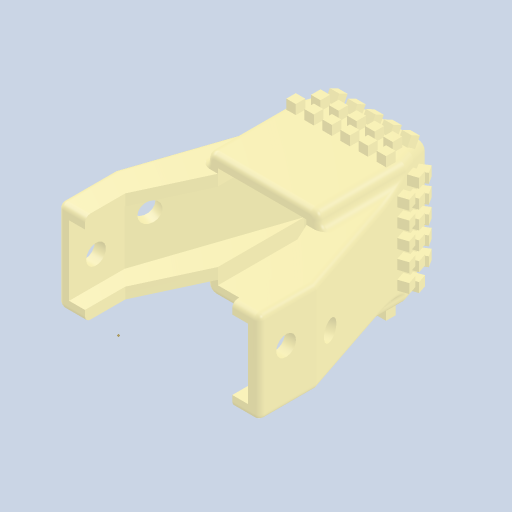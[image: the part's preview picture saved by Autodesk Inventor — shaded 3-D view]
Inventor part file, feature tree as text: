
AUTODESK INVENTOR PART (.ipt)
format: ipt  version: 2023 (Build 270158000, 158)  size: 1,275,904 bytes
history: native  units: mm
features: other x27, extrude x18, fillet x3, mirror x2, loft x1, pattern_circular x1
ambient origin geometry x8: Origin, YZ Plane, XZ Plane, XY Plane, X Axis, Y Axis, Z Axis, Center Point
bodies: Solid1 (feature_tree)
feature tree (52):
  other  "NP2-Alpha_Payload.ipt"
  other  "Sk:Params"
  extrude  "Ex:FrontSide"  Depth=10.0mm
  extrude  "Ex:FrontLip"  Depth=2.2mm
  other  "EndPlane"
  other  "SidePlane1"
  other  "Sk:EndCone"
  other  "Sk:MiddleLift"
  extrude  "Ex:MiddleLift"  TaperAngle=0.0deg  [1 undecoded]
  extrude  "Ex:FrontLift"  Depth=0.7mm
  loft  "Loft:EndCone"
  other  "FrontPlane"
  other  "SidePlane2"
  fillet  "Fillet:CircularEnd"  Radius=0.8mm
  other  "AnglePlane1"
  other  "Sk:AngleNub1"
  extrude  "Ex:AngleNub1-1"  TaperAngle=0.0deg  [1 undecoded]
  extrude  "Ex:AngleNub1-2"  Depth=0.2mm
  extrude  "Ex:AngleNub1-3"  TaperAngle=0.0deg  [1 undecoded]
  extrude  "Ex:AngleNub1-4"  Depth=0.7mm
  other  "AnglePlane2"
  other  "Sk:AngleNub2"
  extrude  "Ex:AngleNub2-1"  Depth=0.7mm
  extrude  "Ex:AngleNub2-2"  Depth=5.0mm
  extrude  "Ex:AngleNub2-3"  Depth=0.2mm
  extrude  "Ex:AngleNub2-4"  Depth=0.25mm
  extrude  "Ex:SideNub1"  Depth=0.1mm
  other  "Sk:SideNub2"
  extrude  "Ex:SideNub2"  Depth=0.7mm
  fillet  "Fillet:Cleanup"  Radius=3.5mm
  mirror  "Mirror1"
  mirror  "Mirror2"
  other  "SidePlane3"
  extrude  "Ex:UpperHole"  TaperAngle=0.0deg  [1 undecoded]
  extrude  "Ex:LowerHole"  Depth=0.2mm
  pattern_circular  "Pat:ReverseHoles"  [2 undecoded]
  fillet  "Fillet:Final"  Radius=0.2mm
  other  "SlicePlane1"
  other  "SlicePlane2"
  extrude  "Ex:Slice1"  Depth=0.2mm
  extrude  "Ex:Slice2"  Depth=20.0mm
  other  "TaggingFeature1"
  other  "Sk: Base"
  other  "Sk:FrontLip"
  other  "Sk:UpperHole"
  other  "Sk:LowerHole"
  other  "Sk:SideNub1"
  other  "Edges4"
  other  "Sk:Slice1"
  other  "Sk:Slice2"
  other  "Solid1::Payload_NP2_Alpha.ipt"
  other  "Srf1"
note: 6 required parameter values undecoded (feature->parameter linkage not recoverable at this tier; creation-order binding heuristic only, values carry confidence <= 0.55)
